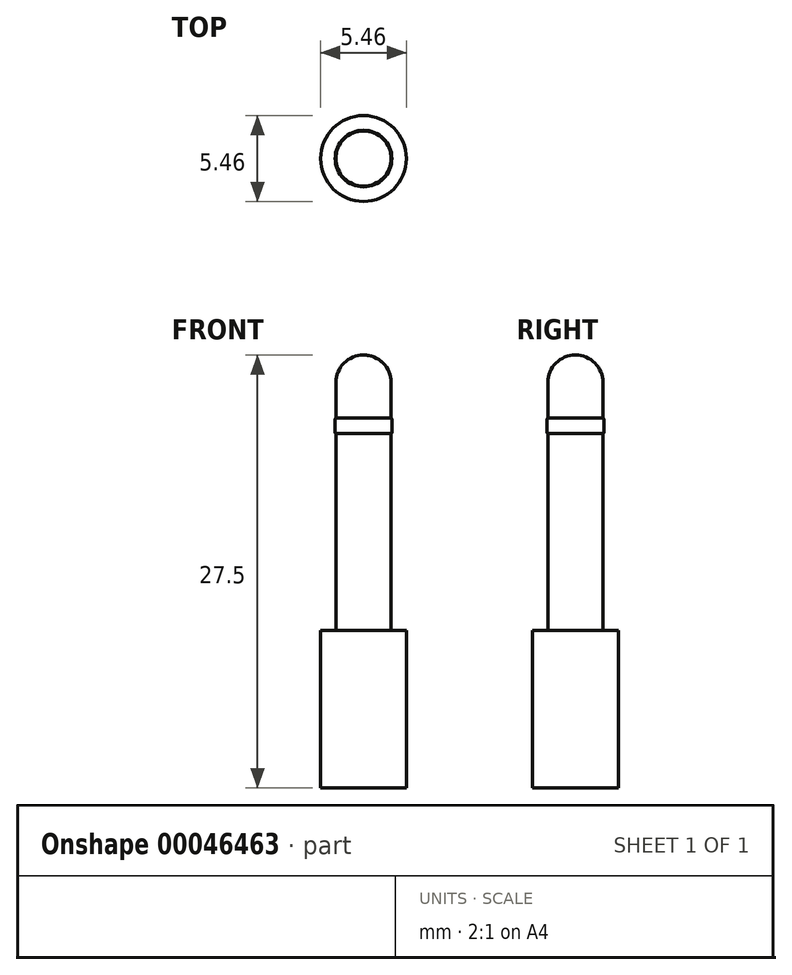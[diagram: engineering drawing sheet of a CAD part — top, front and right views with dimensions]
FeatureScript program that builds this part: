
annotation { "Feature Type Name" : "Feature", "Feature Type Description" : "" }
export const myFeature = defineFeature(function(context is Context, id is Id, definition is map)
    precondition{}
    {
        {
            var Q0;
            Q0=qCreatedBy(makeId("Top.planeOp"),FACE);
            var sketch = newSketch(context, id + "F0", { "sketchPlane" : qUnion([Q0])});
            skCircle(sketch, "E0", {"center": v(0, 0) * mm, "radius": 2.73 * mm});
            skSolve(sketch);
        }
        {
            var Q0;
            Q0=makeQuery(id+"F0.imprint","IMPRINT",FACE,{"disambiguationData":[TD([[makeQuery(id+"F0.imprint","IMPRINT",EDGE,{"derivedFrom":sQuery(id+"F0.wireOp",EDGE,"E0")}),1.0]])]});
            extrude(context, id + "F1", {"entities" : qUnion([Q0]), "depth" : 10 * mm});
        }
        {
            var Q0;
            Q0=makeQuery(id+"F1.opExtrude","CAP_FACE",FACE,{"disambiguationData":[OSD([sQuery(id+"F0.wireOp",EDGE,"E0")])],"isStart":false});
            var sketch = newSketch(context, id + "F2", { "sketchPlane" : qUnion([Q0])});
            skPoint(sketch, "E1", {"position": v(0, 0) * mm});
            skCircle(sketch, "E2", {"center": v(0, 0) * mm, "radius": 1.75 * mm});
            skSolve(sketch);
        }
        {
            var Q0;
            Q0=makeQuery(id+"F2.imprint","IMPRINT",FACE,{"disambiguationData":[TD([[makeQuery(id+"F2.imprint","IMPRINT",EDGE,{"derivedFrom":sQuery(id+"F2.wireOp",EDGE,"E2")}),1.0]])]});
            extrude(context, id + "F3", {"entities" : qUnion([Q0]), "operationType" : NewBodyOperationType.ADD, "depth" : 12.5 * mm});
        }
        {
            var Q0;
            Q0=makeQuery(id+"F3.opExtrude","CAP_FACE",FACE,{"disambiguationData":[OSD([sQuery(id+"F2.wireOp",EDGE,"E2")])],"isStart":false});
            var sketch = newSketch(context, id + "F4", { "sketchPlane" : qUnion([Q0])});
            skPoint(sketch, "E3", {"position": v(0, 0) * mm});
            skCircle(sketch, "E4", {"center": v(0, 0) * mm, "radius": 1.8 * mm});
            skSolve(sketch);
        }
        {
            var Q0;
            Q0=makeQuery(id+"F4.imprint","IMPRINT",FACE,{"disambiguationData":[TD([[makeQuery(id+"F4.imprint","IMPRINT",EDGE,{"derivedFrom":makeQuery(id+"F3.opExtrude","CAP_EDGE",EDGE,{"disambiguationData":[OSD([sQuery(id+"F2.wireOp",EDGE,"E2")])],"isStart":false})}),1.0]])]});
            var Q1;
            Q1=makeQuery(id+"F4.imprint","IMPRINT",FACE,{"disambiguationData":[TD([[makeQuery(id+"F4.imprint","IMPRINT",EDGE,{"derivedFrom":sQuery(id+"F4.wireOp",EDGE,"E4")}),1.0]])]});
            extrude(context, id + "F5", {"entities" : qUnion([Q0, Q1]), "operationType" : NewBodyOperationType.ADD, "depth" : 1 * mm});
        }
        {
            var Q0;
            Q0=makeQuery(id+"F5.opExtrude","CAP_FACE",FACE,{"disambiguationData":[OSD([sQuery(id+"F4.wireOp",EDGE,"E4")])],"isStart":false});
            var sketch = newSketch(context, id + "F6", { "sketchPlane" : qUnion([Q0])});
            skPoint(sketch, "E5", {"position": v(0, 0) * mm});
            skCircle(sketch, "E6", {"center": v(0, 0) * mm, "radius": 1.75 * mm});
            skSolve(sketch);
        }
        {
            var Q0;
            Q0=makeQuery(id+"F6.imprint","IMPRINT",FACE,{"disambiguationData":[TD([[makeQuery(id+"F6.imprint","IMPRINT",EDGE,{"derivedFrom":sQuery(id+"F6.wireOp",EDGE,"E6")}),1.0]])]});
            extrude(context, id + "F7", {"entities" : qUnion([Q0]), "operationType" : NewBodyOperationType.ADD, "depth" : 4 * mm});
        }
        {
            var Q0;
            Q0=makeQuery(id+"F5.opExtrude","CAP_EDGE",EDGE,{"disambiguationData":[OSD([sQuery(id+"F4.wireOp",EDGE,"E4")])],"isStart":false});
            var Q1;
            Q1=makeQuery(id+"F5.opExtrude","CAP_EDGE",EDGE,{"disambiguationData":[OSD([sQuery(id+"F4.wireOp",EDGE,"E4")])],"isStart":true});
            fillet(context, id + "F8", {"entities" : qUnion([Q0, Q1]), "radius" : .1 * mm, "tangentPropagation" : true, "allowEdgeOverflow" : false});
        }
        {
            var Q0;
            Q0=makeQuery(id+"F7.opExtrude","CAP_EDGE",EDGE,{"disambiguationData":[OSD([sQuery(id+"F6.wireOp",EDGE,"E6")])],"isStart":false});
            fillet(context, id + "F9", {"entities" : qUnion([Q0]), "radius" : 1.75 * mm, "tangentPropagation" : true, "allowEdgeOverflow" : false});
        }
    });
